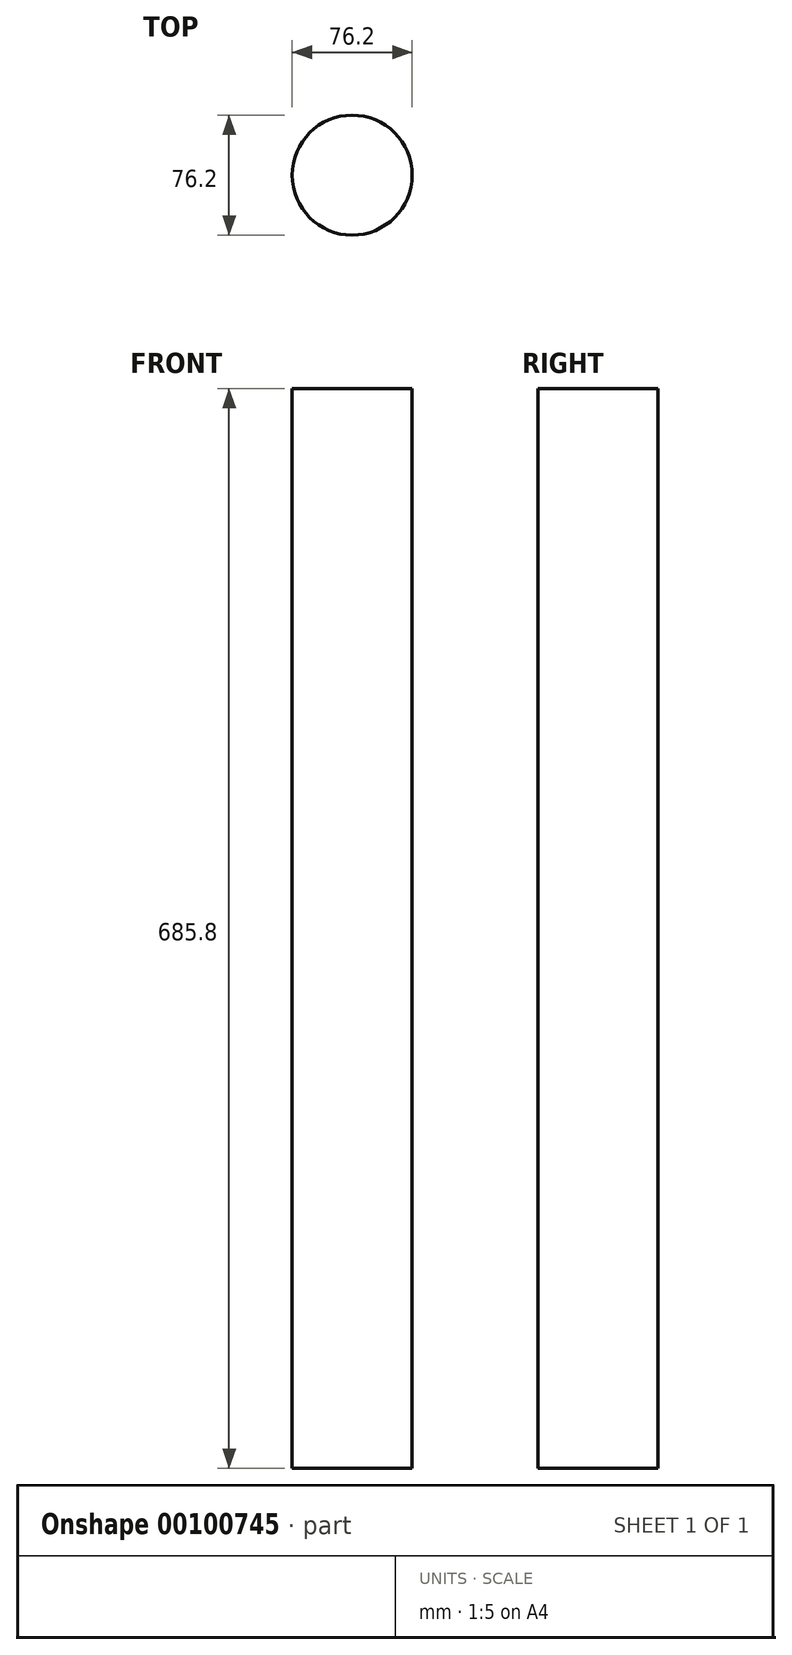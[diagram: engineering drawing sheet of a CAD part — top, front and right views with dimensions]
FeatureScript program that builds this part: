
annotation { "Feature Type Name" : "Feature", "Feature Type Description" : "" }
export const myFeature = defineFeature(function(context is Context, id is Id, definition is map)
    precondition{}
    {
        {
            var Q0;
            Q0=qCreatedBy(makeId("Top.planeOp"),FACE);
            var sketch = newSketch(context, id + "F0", { "sketchPlane" : qUnion([Q0])});
            skCircle(sketch, "E0", {"center": v(0, 0) * mm, "radius": 38.1 * mm});
            skSolve(sketch);
        }
        {
            var Q0;
            Q0 = qSketchRegion(id + "F0", true);
            extrude(context, id + "F1", {"entities" : qUnion([Q0]), "depth" : 685.8 * mm});
        }
    });
